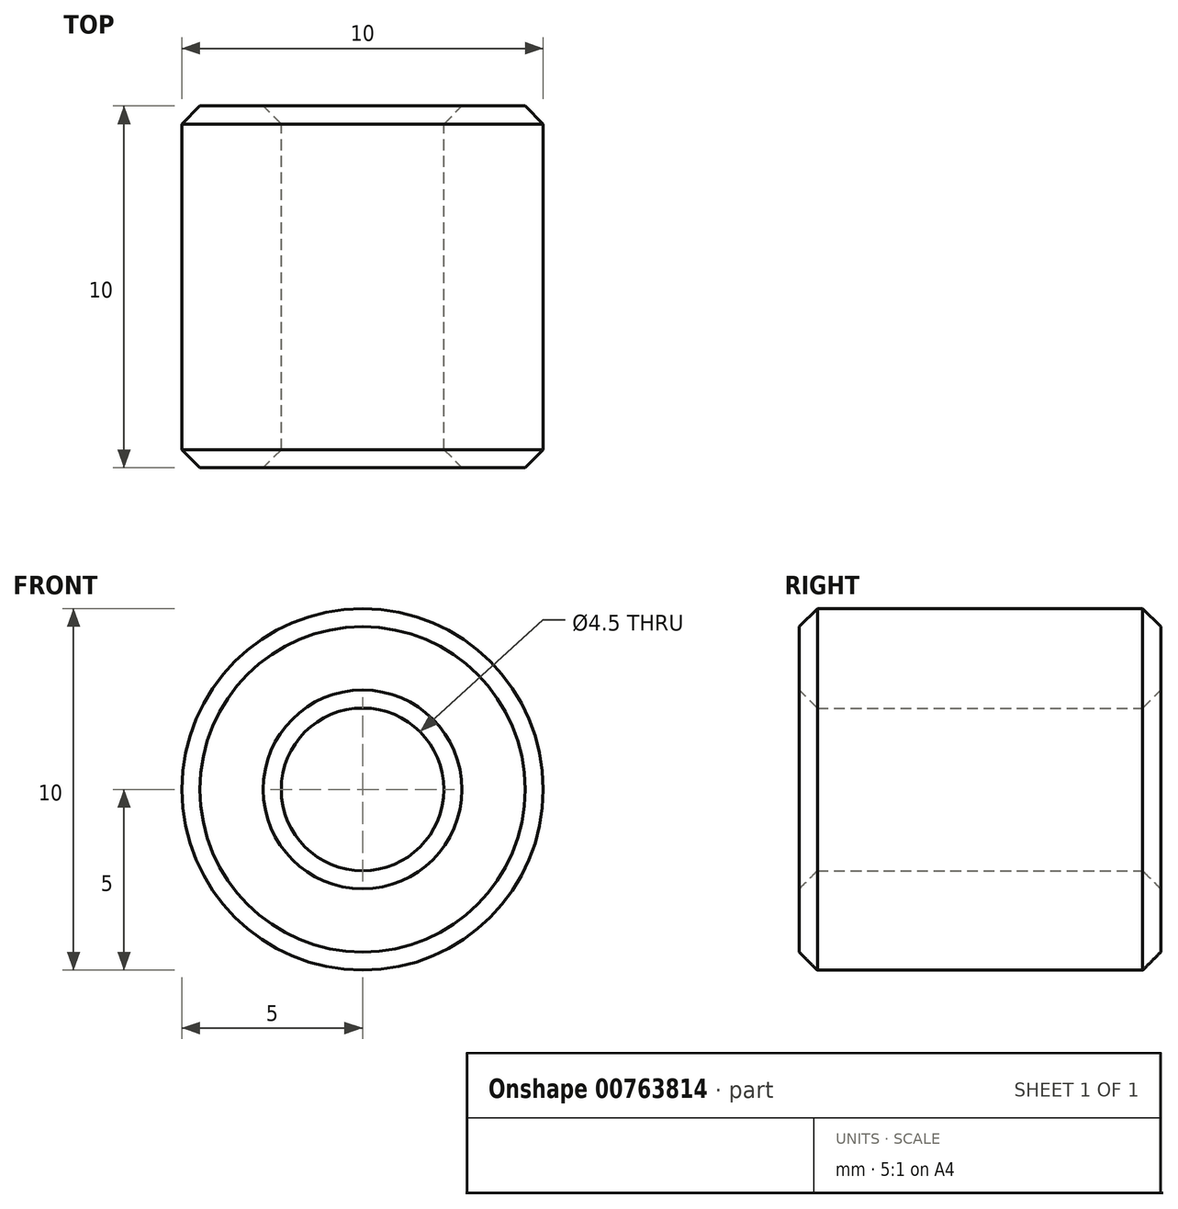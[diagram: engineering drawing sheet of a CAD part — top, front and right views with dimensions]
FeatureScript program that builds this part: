
annotation { "Feature Type Name" : "Feature", "Feature Type Description" : "" }
export const myFeature = defineFeature(function(context is Context, id is Id, definition is map)
    precondition{}
    {
        {
            var Q0;
            Q0=qCreatedBy(makeId("Front.planeOp"),FACE);
            var sketch = newSketch(context, id + "F0", { "sketchPlane" : qUnion([Q0])});
            skCircle(sketch, "E0", {"center": v(0, 0) * mm, "radius": 5 * mm});
            skCircle(sketch, "E1", {"center": v(0, 0) * mm, "radius": 2.25 * mm});
            skSolve(sketch);
        }
        {
            var Q0;
            Q0=makeQuery(id+"F0.imprint","IMPRINT",FACE,{"disambiguationData":[TD([[makeQuery(id+"F0.imprint","IMPRINT",EDGE,{"derivedFrom":sQuery(id+"F0.wireOp",EDGE,"E0")}),1.0]])]});
            extrude(context, id + "F1", {"entities" : qUnion([Q0]), "endBound" : BoundingType.SYMMETRIC, "depth" : 10 * mm, "offsetDistance" : 25 * mm});
        }
        {
            var Q0;
            Q0=makeQuery(id+"F1.opExtrude","CAP_EDGE",EDGE,{"disambiguationData":[OSD([sQuery(id+"F0.wireOp",EDGE,"E0")])],"isStart":false});
            var Q1;
            Q1=makeQuery(id+"F1.opExtrude","CAP_EDGE",EDGE,{"disambiguationData":[OSD([sQuery(id+"F0.wireOp",EDGE,"E1")])],"isStart":false});
            var Q2;
            Q2=makeQuery(id+"F1.opExtrude","CAP_EDGE",EDGE,{"disambiguationData":[OSD([sQuery(id+"F0.wireOp",EDGE,"E0")])],"isStart":true});
            var Q3;
            Q3=makeQuery(id+"F1.opExtrude","CAP_EDGE",EDGE,{"disambiguationData":[OSD([sQuery(id+"F0.wireOp",EDGE,"E1")])],"isStart":true});
            chamfer(context, id + "F2", {"entities" : qUnion([Q0, Q1, Q2, Q3]), "width" : 0.5 * mm, "tangentPropagation" : true});
        }
    });
